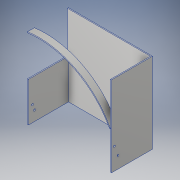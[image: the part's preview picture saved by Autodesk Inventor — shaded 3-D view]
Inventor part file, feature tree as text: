
AUTODESK INVENTOR PART (.ipt)
format: ipt  version: 2019 (Build 230136000, 136)  size: 158,720 bytes
history: native  units: in
note: dims shown in document units (in); Inventor stores cm internally (conversion verified against a paired STEP export)
features: sketch x6, extrude x4, hole x2
ambient origin geometry x8: Origin, YZ Plane, XZ Plane, XY Plane, X Axis, Y Axis, Z Axis, Center Point
bodies: Solid1 (feature_tree)
feature tree (12):
  extrude  "Extrusion1"  Depth=5.896in
  extrude  "Extrusion2"  Depth=0.073in
  extrude  "Extrusion3"  Depth=6.0in
  extrude  "Extrusion7"  Depth=3.0in
  hole  "Hole1"  [1 undecoded]
  hole  "Hole2"  [1 undecoded]
  sketch  "Sketch1"  dims[d0=6.146in d1=5.896in]
  sketch  "Sketch2"  dims[d2=3.0in d3=0.0in d4=0.073in]
  sketch  "Sketch3"  dims[d5=0.073in d6=6.0in]
  sketch  "Sketch9"  dims[d7=9.0in d8=0.0in d9=3.0in]
  sketch  "Sketch10"  dims[d10=2.927in d11=0.0in d23=0.073in]
  sketch  "Sketch11"  dims[d24=0.073in d25=0.5in d26=0.0in d27=0.731in d28=0.441in d29=0.289in d30=1.15in d31=0.146in d32=0.38in d33=0.375in d34=0.25in d35=0.5635in d36=0.588in d37=0.8108in d38=1.581in d39=0.213in d40=0.477in d41=0.857in d42=0.146in d43=0.38in d44=0.375in d45=0.25in d46=0.5635in d47=0.588in d48=0.8108in d49=6.146in d50=0.0365in d51=3.15in]
note: 2 required parameter values undecoded (feature->parameter linkage not recoverable at this tier; creation-order binding heuristic only, values carry confidence <= 0.55)
